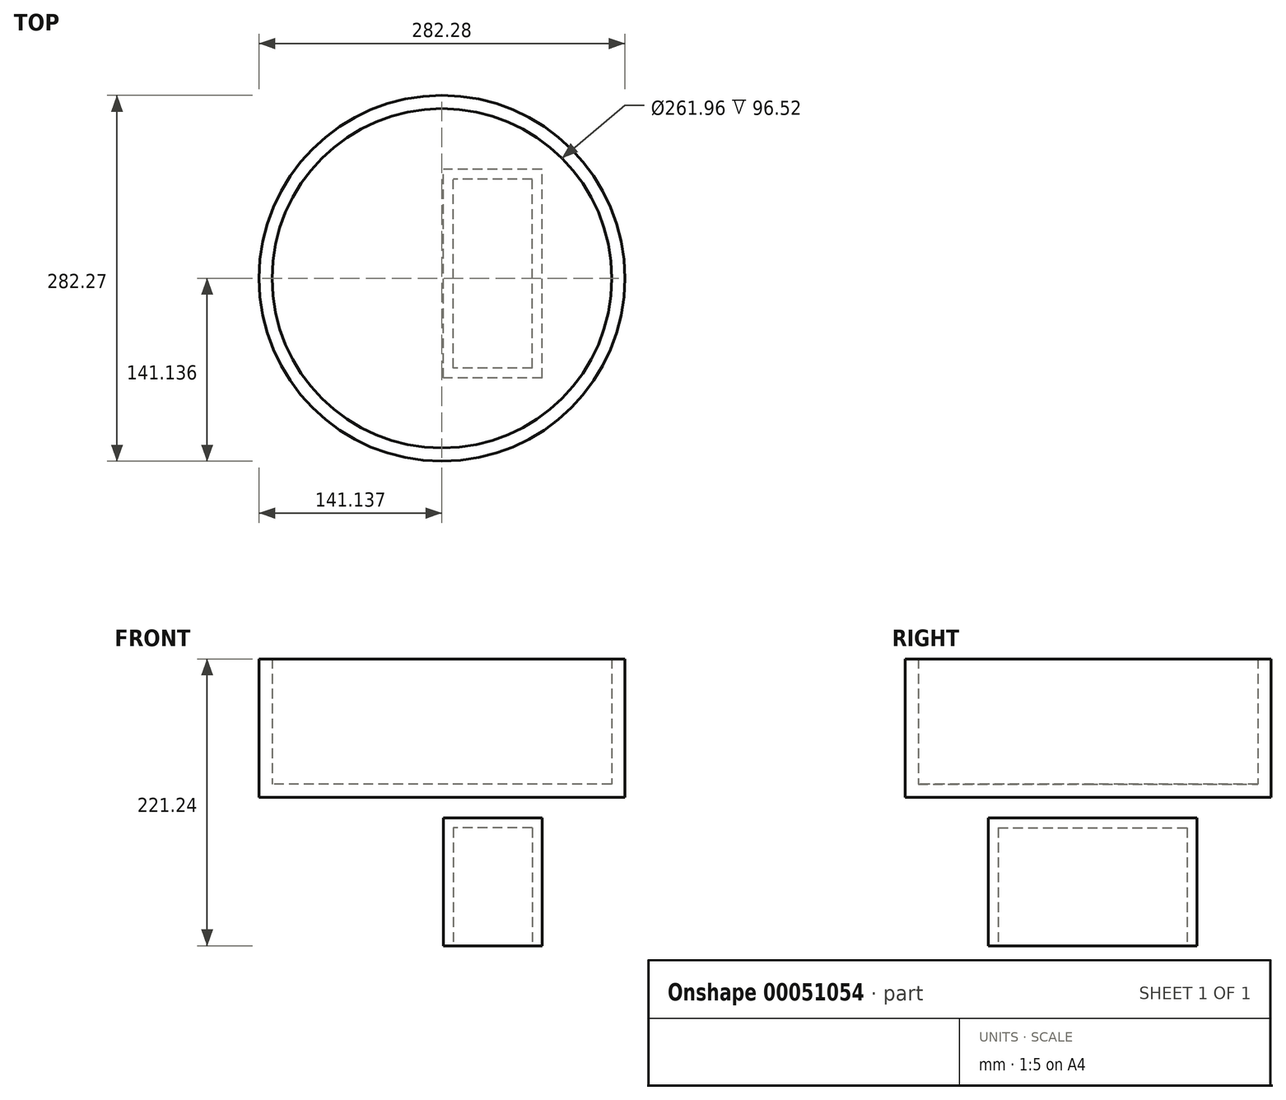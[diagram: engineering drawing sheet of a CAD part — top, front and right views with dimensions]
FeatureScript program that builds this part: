
annotation { "Feature Type Name" : "Feature", "Feature Type Description" : "" }
export const myFeature = defineFeature(function(context is Context, id is Id, definition is map)
    precondition{}
    {
        {
            var Q0;
            Q0=qCreatedBy(makeId("Top.planeOp"),FACE);
            var sketch = newSketch(context, id + "F0", { "sketchPlane" : qUnion([Q0])});
            skCircle(sketch, "E0", {"center": v(-1, 0.5) * mm, "radius": 141.14 * mm});
            skSolve(sketch);
        }
        {
            var Q0;
            Q0 = qSketchRegion(id + "F0", true);
            extrude(context, id + "F1", {"entities" : qUnion([Q0]), "depth" : 106.68 * mm});
        }
        {
            var Q0;
            Q0=makeQuery(id+"F1.opExtrude","CAP_FACE",FACE,{"disambiguationData":[OSD([sQuery(id+"F0.wireOp",EDGE,"E0")])],"isStart":false});
            shell(context, id + "F2", {"entities" : qUnion([Q0]), "thickness" : 10.16 * mm});
        }
        {
            var Q0;
            Q0=qCreatedBy(makeId("Right.planeOp"),FACE);
            var sketch = newSketch(context, id + "F3", { "sketchPlane" : qUnion([Q0])});
            skLineSegment(sketch, "E1.bottom", {"start": v(-76.3, -15.94) * mm, "end": v(84.5, -15.94) * mm});
            skLineSegment(sketch, "E1.top", {"start": v(-76.3, -114.56) * mm, "end": v(84.5, -114.56) * mm});
            skLineSegment(sketch, "E1.left", {"start": v(-76.3, -15.94) * mm, "end": v(-76.3, -114.56) * mm});
            skLineSegment(sketch, "E1.right", {"start": v(84.5, -15.94) * mm, "end": v(84.5, -114.56) * mm});
            skSolve(sketch);
        }
        {
            var Q0;
            Q0 = qSketchRegion(id + "F3", true);
            extrude(context, id + "F4", {"entities" : qUnion([Q0]), "depth" : 76.2 * mm});
        }
        {
            var Q0;
            Q0=makeQuery(id+"F4.opExtrude","SWEPT_FACE",FACE,{"disambiguationData":[OSD([sQuery(id+"F3.wireOp",EDGE,"E1.top")])]});
            shell(context, id + "F5", {"entities" : qUnion([Q0]), "thickness" : 7.62 * mm});
        }
    });
